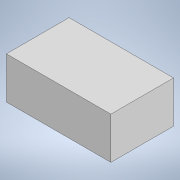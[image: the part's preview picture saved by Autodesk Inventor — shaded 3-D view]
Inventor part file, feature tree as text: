
AUTODESK INVENTOR PART (.ipt)
format: ipt  version: 2020.2 (Build 242310000, 310)  size: 86,528 bytes
history: native  units: mm
features: extrude x1, sketch x1
ambient origin geometry x8: Origin, YZ Plane, XZ Plane, XY Plane, X Axis, Y Axis, Z Axis, Center Point
bodies: Solide1 (feature_tree)
feature tree (2):
  extrude  "Extrusion1"  Depth=50.0mm
  sketch  "Esquisse1"
